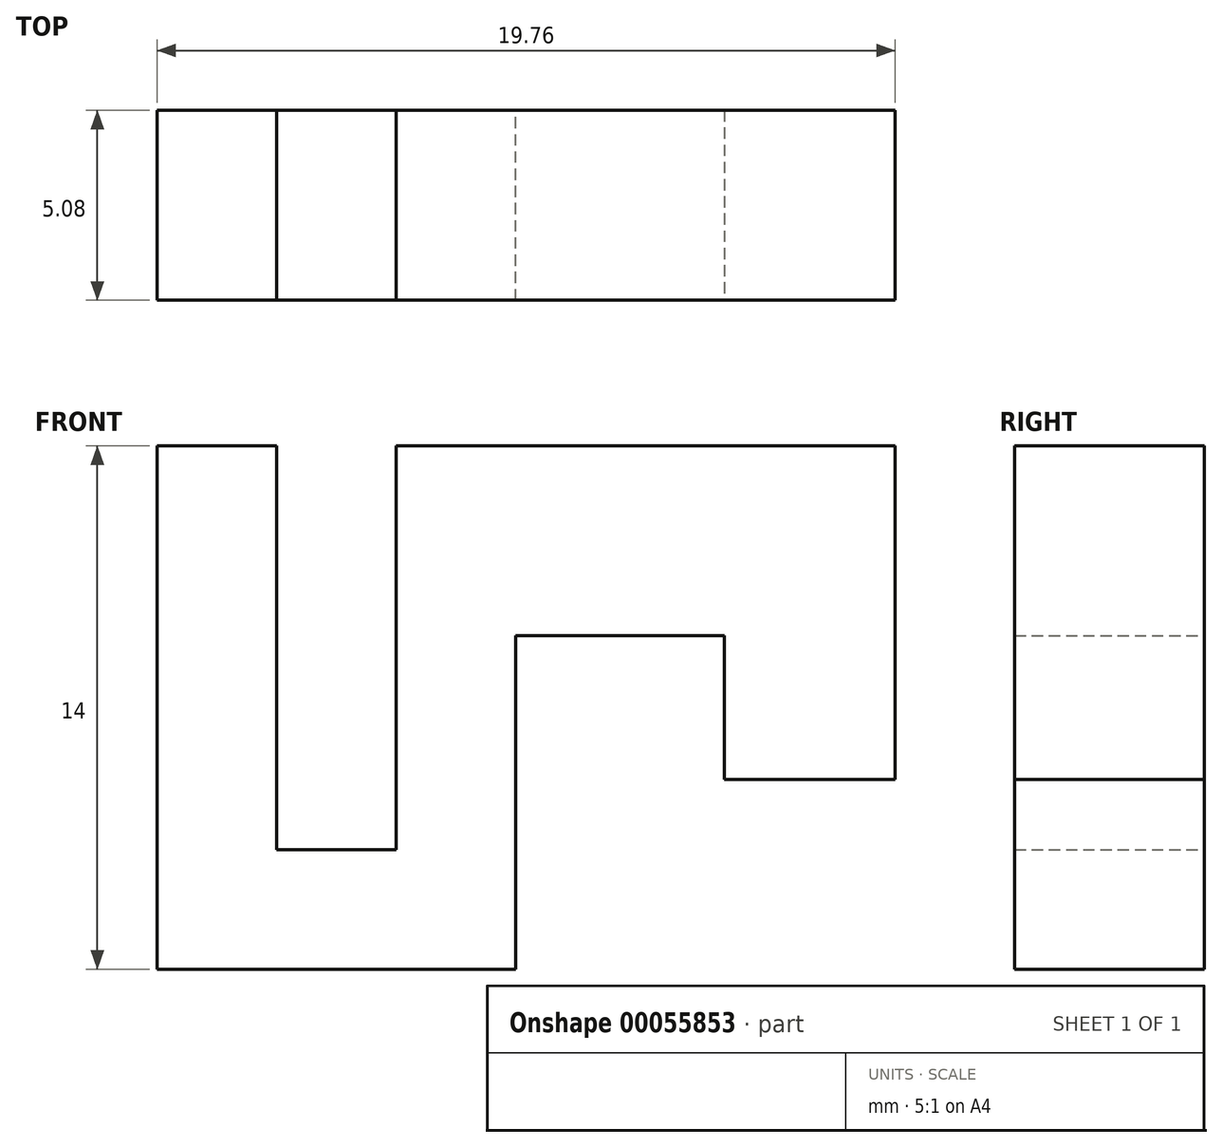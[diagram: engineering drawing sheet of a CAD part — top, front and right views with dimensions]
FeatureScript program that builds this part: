
annotation { "Feature Type Name" : "Feature", "Feature Type Description" : "" }
export const myFeature = defineFeature(function(context is Context, id is Id, definition is map)
    precondition{}
    {
        {
            var Q0;
            Q0=qCreatedBy(makeId("Front.planeOp"),FACE);
            var sketch = newSketch(context, id + "F0", { "sketchPlane" : qUnion([Q0])});
            skLineSegment(sketch, "E0.bottom", {"start": v(1.27, 0) * mm, "end": v(3.2, 0) * mm});
            skLineSegment(sketch, "E0.top", {"start": v(1.27, 14) * mm, "end": v(3.2, 14) * mm});
            skLineSegment(sketch, "E0.left", {"start": v(0, 1.27) * mm, "end": v(0, 12.73) * mm});
            skLineSegment(sketch, "E0.right", {"start": v(3.2, 0) * mm, "end": v(3.2, 14) * mm});
            skLineSegment(sketch, "E1.bottom", {"start": v(3.2, 0) * mm, "end": v(6.4, 0) * mm});
            skLineSegment(sketch, "E1.top", {"start": v(3.2, 3.2) * mm, "end": v(6.4, 3.2) * mm});
            skLineSegment(sketch, "E1.left", {"start": v(3.2, 0) * mm, "end": v(3.2, 3.2) * mm});
            skLineSegment(sketch, "E1.right", {"start": v(6.4, 0) * mm, "end": v(6.4, 3.2) * mm});
            skLineSegment(sketch, "E2.bottom", {"start": v(6.4, 0) * mm, "end": v(8.33, 0) * mm});
            skLineSegment(sketch, "E2.top", {"start": v(6.4, 14) * mm, "end": v(9.6, 14) * mm});
            skLineSegment(sketch, "E2.left", {"start": v(6.4, 0) * mm, "end": v(6.4, 14) * mm});
            skLineSegment(sketch, "E2.right", {"start": v(9.6, 1.27) * mm, "end": v(9.6, 14) * mm});
            skLineSegment(sketch, "E3.bottom", {"start": v(9.6, 14) * mm, "end": v(19.76, 14) * mm});
            skLineSegment(sketch, "E3.top", {"start": v(9.6, 8.92) * mm, "end": v(19.76, 8.92) * mm});
            skLineSegment(sketch, "E3.left", {"start": v(9.6, 14) * mm, "end": v(9.6, 8.92) * mm});
            skLineSegment(sketch, "E3.right", {"start": v(19.76, 14) * mm, "end": v(19.76, 8.92) * mm});
            skPoint(sketch, "E4.visualSharp", {"position": v(0, 14) * mm});
            skArc(sketch, "E4.filletArc", {"start": v(1.27, 14) * mm, "mid": v(0.37, 13.63) * mm, "end": v(0, 12.73) * mm});
            skPoint(sketch, "E5.visualSharp", {"position": v(0, 0) * mm});
            skArc(sketch, "E5.filletArc", {"start": v(0, 1.27) * mm, "mid": v(0.37, 0.37) * mm, "end": v(1.27, 0) * mm});
            skPoint(sketch, "E6.visualSharp", {"position": v(9.6, 0) * mm});
            skArc(sketch, "E6.filletArc", {"start": v(8.33, 0) * mm, "mid": v(9.23, 0.37) * mm, "end": v(9.6, 1.27) * mm});
            skLineSegment(sketch, "E7", {"start": v(0, 10.8) * mm, "end": v(3.2, 10.8) * mm});
            skLineSegment(sketch, "E8", {"start": v(0, 0) * mm, "end": v(0, 1.27) * mm});
            skLineSegment(sketch, "E9", {"start": v(0, 0) * mm, "end": v(1.27, 0) * mm});
            skLineSegment(sketch, "E10", {"start": v(9.6, 0) * mm, "end": v(8.33, 0) * mm});
            skLineSegment(sketch, "E11", {"start": v(9.6, 0) * mm, "end": v(9.6, 1.27) * mm});
            skLineSegment(sketch, "E12", {"start": v(0, 12.73) * mm, "end": v(0, 14) * mm});
            skLineSegment(sketch, "E13", {"start": v(1.27, 14) * mm, "end": v(0, 14) * mm});
            skSolve(sketch);
        }
        {
            var Q0;
            Q0=makeQuery(id+"F0.imprint","IMPRINT",FACE,{"disambiguationData":[TD([[makeQuery(id+"F0.imprint","IMPRINT",EDGE,{"derivedFrom":sQuery(id+"F0.wireOp",EDGE,"E3.bottom")}),-1.0]])]});
            var Q1;
            Q1=makeQuery(id+"F0.imprint","IMPRINT",FACE,{"disambiguationData":[TD([[makeQuery(id+"F0.imprint","IMPRINT",EDGE,{"derivedFrom":sQuery(id+"F0.wireOp",EDGE,"E0.bottom")}),1.0]])]});
            var Q2;
            {var subQ0=sQuery(id+"F0.wireOp",EDGE,"E1.bottom");Q2=makeQuery(id+"F0.imprint","IMPRINT",FACE,{"disambiguationData":[TD([[makeQuery(id+"F0.imprint","IMPRINT",EDGE,{"derivedFrom":subQ0}),1.0]])]});}
            var Q3;
            {var subQ3=sQuery(id+"F0.wireOp",EDGE,"E2.bottom");Q3=makeQuery(id+"F0.imprint","IMPRINT",FACE,{"disambiguationData":[TD([[makeQuery(id+"F0.imprint","IMPRINT",EDGE,{"derivedFrom":subQ3}),1.0]])]});}
            var Q4;
            Q4=makeQuery(id+"F0.imprint","IMPRINT",FACE,{"disambiguationData":[TD([[makeQuery(id+"F0.imprint","IMPRINT",EDGE,{"derivedFrom":sQuery(id+"F0.wireOp",EDGE,"E5.filletArc")}),-1.0]])]});
            var Q5;
            Q5=makeQuery(id+"F0.imprint","IMPRINT",FACE,{"disambiguationData":[TD([[makeQuery(id+"F0.imprint","IMPRINT",EDGE,{"derivedFrom":sQuery(id+"F0.wireOp",EDGE,"E6.filletArc")}),-1.0]])]});
            var Q6;
            {var subQ1=sQuery(id+"F0.wireOp",EDGE,"E0.top");Q6=makeQuery(id+"F0.imprint","IMPRINT",FACE,{"disambiguationData":[TD([[makeQuery(id+"F0.imprint","IMPRINT",EDGE,{"derivedFrom":subQ1}),-1.0]])]});}
            var Q7;
            Q7=makeQuery(id+"F0.imprint","IMPRINT",FACE,{"disambiguationData":[TD([[makeQuery(id+"F0.imprint","IMPRINT",EDGE,{"derivedFrom":sQuery(id+"F0.wireOp",EDGE,"E4.filletArc")}),-1.0]])]});
            extrude(context, id + "F1", {"entities" : qUnion([Q0, Q1, Q2, Q3, Q4, Q5, Q6, Q7]), "depth" : 5.08 * mm});
        }
        {
            var Q0;
            Q0=makeQuery(id+"F1.opExtrude","SWEPT_FACE",FACE,{"disambiguationData":[OSD([sQuery(id+"F0.wireOp",EDGE,"E3.top")])]});
            var sketch = newSketch(context, id + "F2", { "sketchPlane" : qUnion([Q0])});
            skLineSegment(sketch, "E14.bottom", {"start": v(19.76, 5.08) * mm, "end": v(15.19, 5.08) * mm});
            skLineSegment(sketch, "E14.top", {"start": v(19.76, 0) * mm, "end": v(15.19, 0) * mm});
            skLineSegment(sketch, "E14.left", {"start": v(19.76, 5.08) * mm, "end": v(19.76, 0) * mm});
            skLineSegment(sketch, "E14.right", {"start": v(15.19, 0) * mm, "end": v(15.19, 5.08) * mm});
            skSolve(sketch);
        }
        {
            var Q0;
            Q0=makeQuery(id+"F2.imprint","IMPRINT",FACE,{"disambiguationData":[TD([[makeQuery(id+"F2.imprint","IMPRINT",EDGE,{"derivedFrom":sQuery(id+"F2.wireOp",EDGE,"E14.bottom")}),-1.0]])]});
            extrude(context, id + "F3", {"entities" : qUnion([Q0]), "operationType" : NewBodyOperationType.ADD, "depth" : (14 - 2 * 5.08) * mm});
        }
    });
